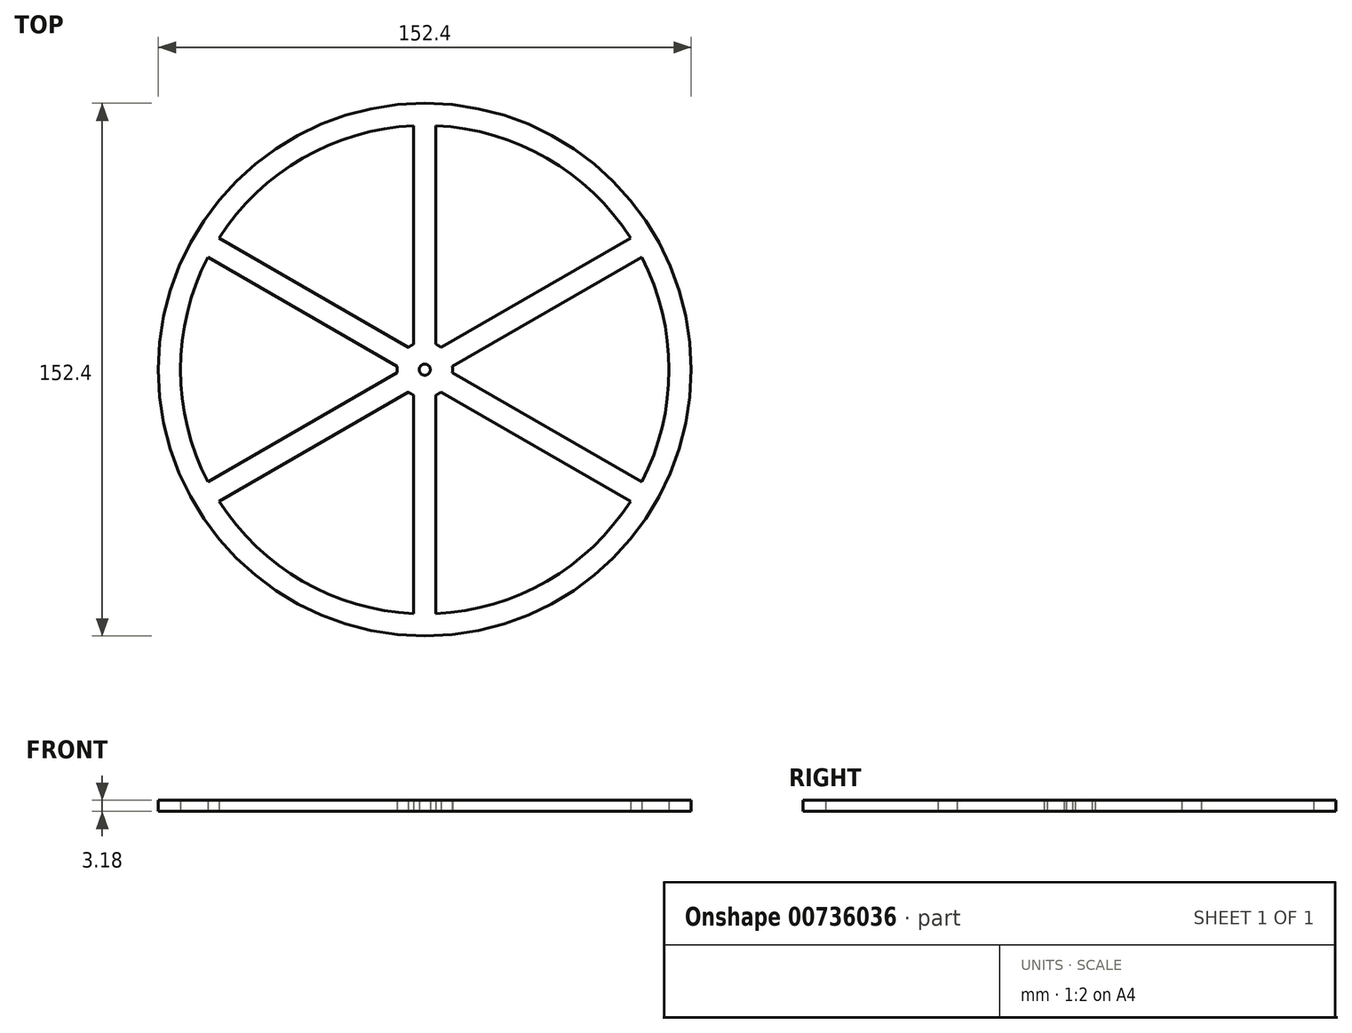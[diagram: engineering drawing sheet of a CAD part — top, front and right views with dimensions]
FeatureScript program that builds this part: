
annotation { "Feature Type Name" : "Feature", "Feature Type Description" : "" }
export const myFeature = defineFeature(function(context is Context, id is Id, definition is map)
    precondition{}
    {
        {
            var Q0;
            Q0=qCreatedBy(makeId("Top.planeOp"),FACE);
            var sketch = newSketch(context, id + "F0", { "sketchPlane" : qUnion([Q0])});
            skCircle(sketch, "E0", {"center": v(0, 0) * mm, "radius": 76.2 * mm});
            skCircle(sketch, "E1", {"center": v(0, 0) * mm, "radius": 1.59 * mm});
            skCircle(sketch, "E2", {"center": v(0, 0) * mm, "radius": 69.85 * mm});
            skCircle(sketch, "E3", {"center": v(0, 0) * mm, "radius": 7.94 * mm});
            skLineSegment(sketch, "E4", {"start": v(-3.17, 7.27) * mm, "end": v(-3.18, 69.78) * mm});
            skLineSegment(sketch, "E5", {"start": v(3.18, 7.27) * mm, "end": v(3.17, 69.78) * mm});
            skLineSegment(sketch, "E6.1.0", {"start": v(-7.89, 0.89) * mm, "end": v(-62.02, 32.14) * mm});
            skLineSegment(sketch, "E6.1.1", {"start": v(-4.71, 6.39) * mm, "end": v(-58.84, 37.64) * mm});
            skLineSegment(sketch, "E6.2.0", {"start": v(-4.71, -6.39) * mm, "end": v(-58.84, -37.64) * mm});
            skLineSegment(sketch, "E6.2.1", {"start": v(-7.89, -0.89) * mm, "end": v(-62.02, -32.14) * mm});
            skLineSegment(sketch, "E6.3.0", {"start": v(3.17, -7.27) * mm, "end": v(3.17, -69.78) * mm});
            skLineSegment(sketch, "E6.3.1", {"start": v(-3.18, -7.27) * mm, "end": v(-3.18, -69.78) * mm});
            skLineSegment(sketch, "E6.4.0", {"start": v(7.89, -0.89) * mm, "end": v(62.02, -32.14) * mm});
            skLineSegment(sketch, "E6.4.1", {"start": v(4.71, -6.39) * mm, "end": v(58.84, -37.64) * mm});
            skLineSegment(sketch, "E6.5.0", {"start": v(4.71, 6.39) * mm, "end": v(58.84, 37.64) * mm});
            skLineSegment(sketch, "E6.5.1", {"start": v(7.89, 0.89) * mm, "end": v(62.02, 32.14) * mm});
            skLineSegment(sketch, "E7", {"start": v(-3.17, 7.27) * mm, "end": v(3.18, 7.27) * mm});
            skSolve(sketch);
        }
        {
            var Q0;
            Q0 = qSketchRegion(id + "F0", true);
            var Q1;
            Q1=makeQuery(id+"F0.imprint","IMPRINT",FACE,{"disambiguationData":[TD([[makeQuery(id+"F0.imprint","IMPRINT",EDGE,{"derivedFrom":sQuery(id+"F0.wireOp",EDGE,"E0")}),1.0]])]});
            var Q2;
            {var subQ0=sQuery(id+"F0.wireOp",EDGE,"E6.1.0");Q2=makeQuery(id+"F0.imprint","IMPRINT",FACE,{"disambiguationData":[TD([[makeQuery(id+"F0.imprint","IMPRINT",EDGE,{"derivedFrom":subQ0}),-1.0]])]});}
            var Q3;
            {var subQ0=sQuery(id+"F0.wireOp",EDGE,"E6.2.0");Q3=makeQuery(id+"F0.imprint","IMPRINT",FACE,{"disambiguationData":[TD([[makeQuery(id+"F0.imprint","IMPRINT",EDGE,{"derivedFrom":subQ0}),-1.0]])]});}
            var Q4;
            Q4=makeQuery(id+"F0.imprint","IMPRINT",FACE,{"disambiguationData":[TD([[makeQuery(id+"F0.imprint","IMPRINT",EDGE,{"derivedFrom":sQuery(id+"F0.wireOp",EDGE,"E1")}),-1.0]])]});
            var Q5;
            {var subQ0=sQuery(id+"F0.wireOp",EDGE,"E6.3.0");Q5=makeQuery(id+"F0.imprint","IMPRINT",FACE,{"disambiguationData":[TD([[makeQuery(id+"F0.imprint","IMPRINT",EDGE,{"derivedFrom":subQ0}),-1.0]])]});}
            var Q6;
            {var subQ0=sQuery(id+"F0.wireOp",EDGE,"E6.4.0");Q6=makeQuery(id+"F0.imprint","IMPRINT",FACE,{"disambiguationData":[TD([[makeQuery(id+"F0.imprint","IMPRINT",EDGE,{"derivedFrom":subQ0}),-1.0]])]});}
            var Q7;
            {var subQ0=sQuery(id+"F0.wireOp",EDGE,"E6.5.0");Q7=makeQuery(id+"F0.imprint","IMPRINT",FACE,{"disambiguationData":[TD([[makeQuery(id+"F0.imprint","IMPRINT",EDGE,{"derivedFrom":subQ0}),-1.0]])]});}
            var Q8;
            {var subQ0=sQuery(id+"F0.wireOp",EDGE,"E4");Q8=makeQuery(id+"F0.imprint","IMPRINT",FACE,{"disambiguationData":[TD([[makeQuery(id+"F0.imprint","IMPRINT",EDGE,{"derivedFrom":subQ0}),-1.0]])]});}
            var Q9;
            {var subQ0=sQuery(id+"F0.wireOp",EDGE,"E7");Q9=makeQuery(id+"F0.imprint","IMPRINT",FACE,{"disambiguationData":[TD([[makeQuery(id+"F0.imprint","IMPRINT",EDGE,{"derivedFrom":subQ0}),1.0]])]});}
            extrude(context, id + "F1", {"entities" : qUnion([Q0, Q1, Q2, Q3, Q4, Q5, Q6, Q7, Q8, Q9]), "depth" : 3.17 * mm, "offsetDistance" : 25.4 * mm});
        }
    });
